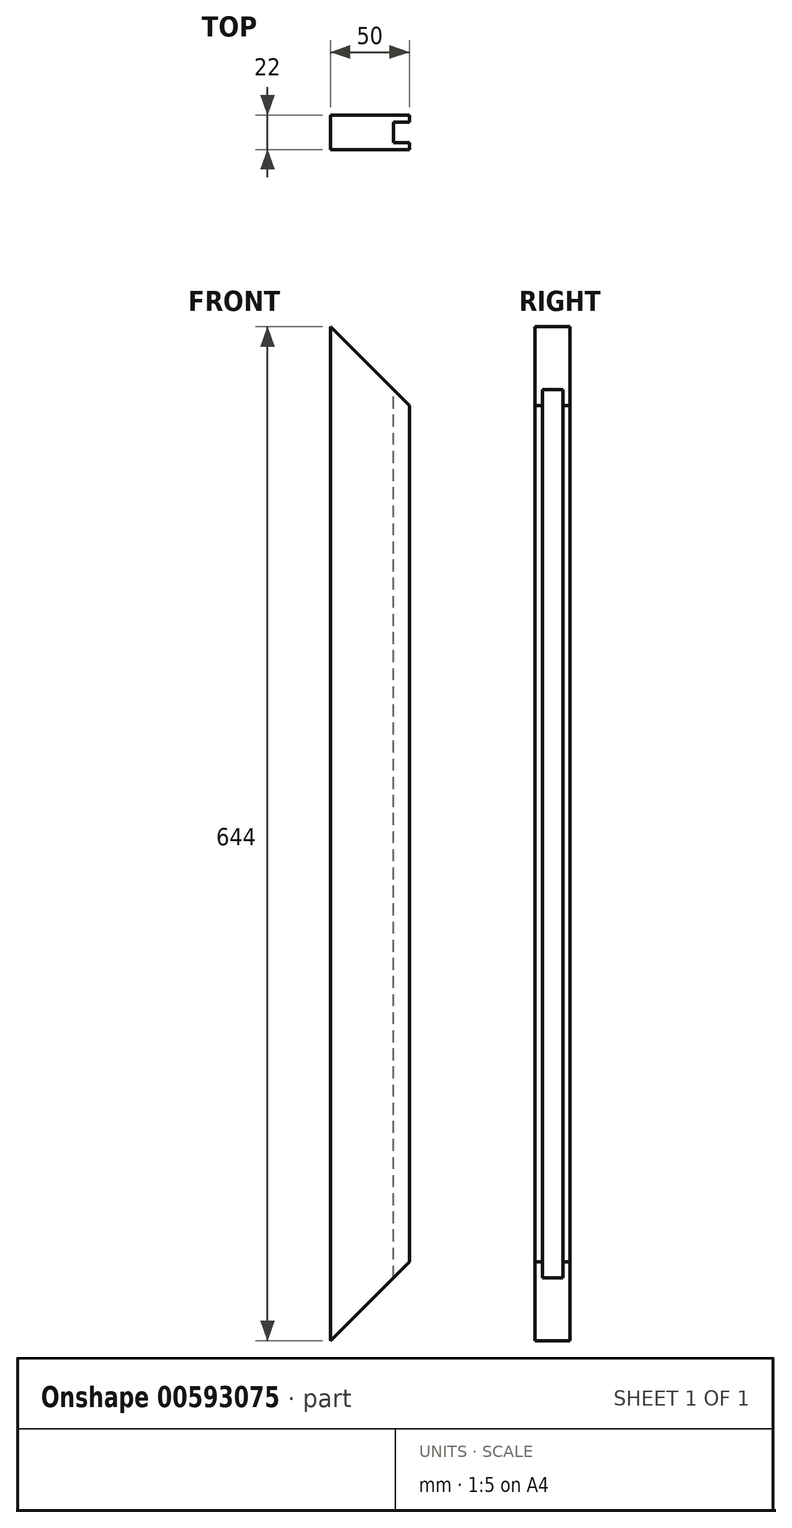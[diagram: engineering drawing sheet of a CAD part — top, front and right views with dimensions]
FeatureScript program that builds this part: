
annotation { "Feature Type Name" : "Feature", "Feature Type Description" : "" }
export const myFeature = defineFeature(function(context is Context, id is Id, definition is map)
    precondition{}
    {
        {
            var Q0;
            Q0=qCreatedBy(makeId("Front.planeOp"),FACE);
            var sketch = newSketch(context, id + "F0", { "sketchPlane" : qUnion([Q0])});
            skLineSegment(sketch, "E0.left", {"start": v(-50, 322) * mm, "end": v(-50, -322) * mm});
            skLineSegment(sketch, "E0.right", {"start": v(0, 272) * mm, "end": v(0, -272) * mm});
            skLineSegment(sketch, "E1", {"start": v(-50, 322) * mm, "end": v(0, 272) * mm});
            skLineSegment(sketch, "E2", {"start": v(-50, -322) * mm, "end": v(0, -272) * mm});
            skSolve(sketch);
        }
        {
            var Q0;
            Q0=makeQuery(id+"F0.imprint","IMPRINT",FACE,{"disambiguationData":[TD([[makeQuery(id+"F0.imprint","IMPRINT",EDGE,{"derivedFrom":sQuery(id+"F0.wireOp",EDGE,"E0.left")}),1.0]])]});
            extrude(context, id + "F1", {"entities" : qUnion([Q0]), "depth" : 22 * mm, "offsetDistance" : 25 * mm});
        }
        {
            var Q0;
            Q0=makeQuery(id+"F1.opExtrude","SWEPT_FACE",FACE,{"disambiguationData":[OSD([sQuery(id+"F0.wireOp",EDGE,"E0.right")])]});
            var sketch = newSketch(context, id + "F2", { "sketchPlane" : qUnion([Q0])});
            skLineSegment(sketch, "E3.bottom", {"start": v(-17.5, -295.8) * mm, "end": v(-4.5, -295.8) * mm});
            skLineSegment(sketch, "E3.top", {"start": v(-17.5, 285.63) * mm, "end": v(-4.5, 285.63) * mm});
            skLineSegment(sketch, "E3.left", {"start": v(-17.5, -295.8) * mm, "end": v(-17.5, 285.63) * mm});
            skLineSegment(sketch, "E3.right", {"start": v(-4.5, -295.8) * mm, "end": v(-4.5, 285.63) * mm});
            skSolve(sketch);
        }
        {
            var Q0;
            Q0 = qSketchRegion(id + "F2", true);
            extrude(context, id + "F3", {"entities" : qUnion([Q0]), "operationType" : NewBodyOperationType.REMOVE, "oppositeDirection" : true, "depth" : 10 * mm, "offsetDistance" : 25 * mm});
        }
    });
